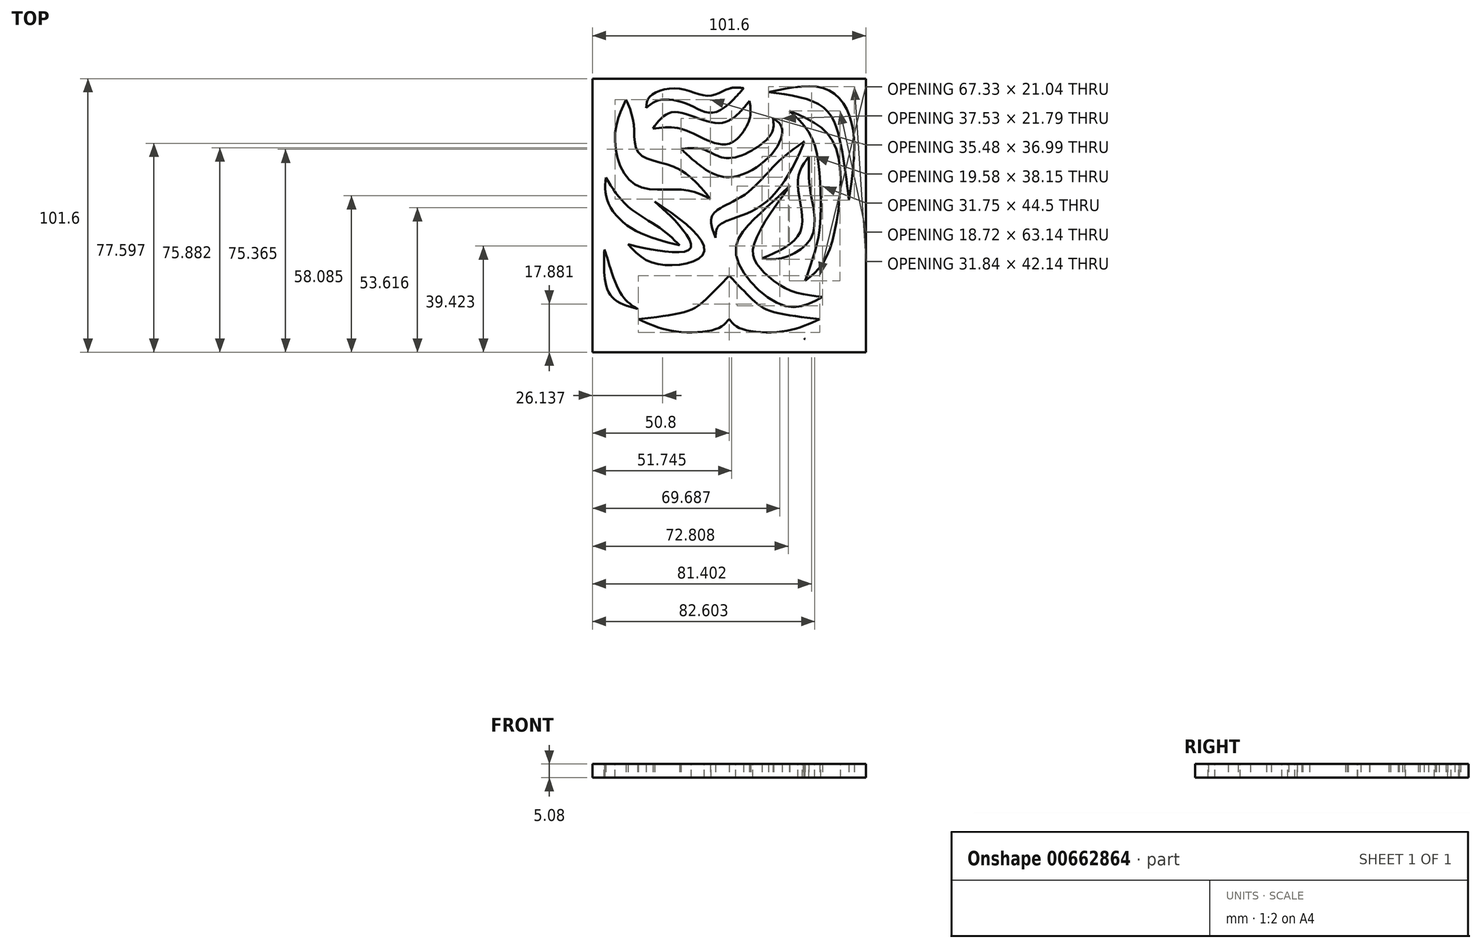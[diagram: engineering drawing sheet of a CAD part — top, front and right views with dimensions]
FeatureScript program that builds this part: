
annotation { "Feature Type Name" : "Feature", "Feature Type Description" : "" }
export const myFeature = defineFeature(function(context is Context, id is Id, definition is map)
    precondition{}
    {
        {
            var Q0;
            Q0=qCreatedBy(makeId("Top.planeOp"),FACE);
            var sketch = newSketch(context, id + "F0", { "sketchPlane" : qUnion([Q0])});
            skLineSegment(sketch, "E0.bottom", {"start": v(50.8, 50.8) * mm, "end": v(-50.8, 50.8) * mm});
            skLineSegment(sketch, "E0.top", {"start": v(50.8, -50.8) * mm, "end": v(-50.8, -50.8) * mm});
            skLineSegment(sketch, "E0.left", {"start": v(50.8, 50.8) * mm, "end": v(50.8, -50.8) * mm});
            skLineSegment(sketch, "E0.right", {"start": v(-50.8, 50.8) * mm, "end": v(-50.8, -50.8) * mm});
            skPoint(sketch, "E0.middle", {"position": v(0, 0) * mm});
            skFitSpline(sketch, "E1", {"points": [v(-38.26, 43.06) * mm, v(-42.4, 28.82) * mm, v(-35, 11.48) * mm, v(-17.34, 9.57) * mm, v(-6.92, 6.07) * mm], "startDerivative": vector(-24.94, -52.93) * mm, "endDerivative": vector(43.77, -22.42) * mm});
            skFitSpline(sketch, "E2", {"points": [v(-38.26, 43.06) * mm, v(-35.4, 33.75) * mm, v(-33.5, 23.1) * mm, v(-19.81, 17.76) * mm, v(-6.92, 6.07) * mm], "startDerivative": vector(17.36, -40) * mm, "endDerivative": vector(39.04, -48.3) * mm});
            skFitSpline(sketch, "E3", {"points": [v(-28.32, 32.16) * mm, v(-20.6, 38.37) * mm, v(-3.58, 34.3) * mm, v(7.55, 42.5) * mm], "startDerivative": vector(22.21, 31.48) * mm, "endDerivative": vector(28.77, 35.63) * mm});
            skFitSpline(sketch, "E4", {"points": [v(7.55, 42.5) * mm, v(7.55, 35.66) * mm, v(0, 26.67) * mm, v(-11.3, 29.46) * mm, v(-20.37, 32.64) * mm, v(-28.32, 32.16) * mm], "startDerivative": vector(6.77, -37) * mm, "endDerivative": vector(-43.42, -6.58) * mm});
            skFitSpline(sketch, "E5", {"points": [v(-17.82, 24.68) * mm, v(-9.31, 24.45) * mm, v(0, 21.26) * mm, v(15.43, 29.93) * mm, v(16.3, 35.98) * mm], "startDerivative": vector(38.3, 4.27) * mm, "endDerivative": vector(-4.66, 29.53) * mm});
            skFitSpline(sketch, "E6", {"points": [v(16.3, 35.98) * mm, v(19.56, 32.8) * mm, v(16.3, 23.33) * mm, v(0, 14.19) * mm, v(-11.46, 19.04) * mm, v(-17.82, 24.68) * mm], "startDerivative": vector(31.19, -18.81) * mm, "endDerivative": vector(-31.98, 30.34) * mm});
            skFitSpline(sketch, "E7", {"points": [v(-45.82, 14.03) * mm, v(-45.26, 5.67) * mm, v(-36.75, -4.5) * mm, v(-18.38, -11.1) * mm], "startDerivative": vector(-2.37, -31.1) * mm, "endDerivative": vector(49.48, -12.28) * mm});
            skFitSpline(sketch, "E8", {"points": [v(-18.38, -11.1) * mm, v(-25.14, -5.06) * mm, v(-37.39, 3.2) * mm, v(-45.82, 14.03) * mm], "startDerivative": vector(-20.78, 21.33) * mm, "endDerivative": vector(-20.77, 32.88) * mm});
            skFitSpline(sketch, "E9", {"points": [v(-27.6, 5.12) * mm, v(-18.54, -3.71) * mm, v(-14.4, -12.38) * mm, v(-28.64, -12.7) * mm, v(-37.47, -10.71) * mm], "startDerivative": vector(33.91, -29.82) * mm, "endDerivative": vector(-32.2, 8.68) * mm});
            skFitSpline(sketch, "E10", {"points": [v(-37.47, -10.71) * mm, v(-30.63, -16.68) * mm, v(-18.78, -18.35) * mm, v(-9.63, -14.53) * mm, v(-11.3, -7.93) * mm, v(-27.6, 5.12) * mm], "startDerivative": vector(33.66, -38) * mm, "endDerivative": vector(-71.79, 48.43) * mm});
            skFitSpline(sketch, "E11", {"points": [v(-43.45, -12.76) * mm, v(-35.26, -21.02) * mm, v(-18.3, -24.64) * mm, v(0, -8.26) * mm], "startDerivative": vector(24.8, -32.16) * mm, "endDerivative": vector(43.21, 55.04) * mm});
            skFitSpline(sketch, "E12", {"points": [v(0, -8.26) * mm, v(-3.36, -19.35) * mm, v(-14.74, -32.4) * mm, v(-26.27, -34.07) * mm, v(-37.14, -27.69) * mm, v(-43.45, -12.76) * mm], "startDerivative": vector(-11.25, -58.13) * mm, "endDerivative": vector(-21.7, 76.53) * mm});
            skFitSpline(sketch, "E13", {"points": [v(-5.03, -8.26) * mm, v(-3.5, -3.55) * mm, v(14.83, 5.94) * mm, v(27.8, 27.47) * mm, v(27.44, 27.11) * mm], "startDerivative": vector(0.93, 29.14) * mm, "endDerivative": vector(-8.43, -11.17) * mm});
            skFitSpline(sketch, "E14", {"points": [v(27.44, 27.11) * mm, v(17.37, 19.06) * mm, v(5.19, 7.32) * mm, v(-6.2, 0) * mm, v(-5.03, -8.26) * mm], "startDerivative": vector(-40.62, -28.64) * mm, "endDerivative": vector(17.62, -44.65) * mm});
            skFitSpline(sketch, "E15", {"points": [v(29.69, 21.9) * mm, v(25.56, 12.69) * mm, v(26.65, -5.5) * mm, v(12.22, -15.95) * mm], "startDerivative": vector(-21.82, -28.94) * mm, "endDerivative": vector(-52.75, -22.05) * mm});
            skFitSpline(sketch, "E16", {"points": [v(12.22, -15.95) * mm, v(19.18, -15.95) * mm, v(30.56, -8.2) * mm, v(30.85, 5.44) * mm, v(29.69, 14) * mm, v(29.69, 21.9) * mm], "startDerivative": vector(37.4, -5.69) * mm, "endDerivative": vector(1.26, 45) * mm});
            skFitSpline(sketch, "E17", {"points": [v(22.51, 10.87) * mm, v(10.77, 0) * mm, v(2.58, -14.28) * mm, v(20.34, -33.49) * mm, v(34.76, -30.23) * mm], "startDerivative": vector(-48.23, -44.33) * mm, "endDerivative": vector(58.75, 32.84) * mm});
            skFitSpline(sketch, "E18", {"points": [v(34.76, -30.23) * mm, v(21.79, -27.47) * mm, v(11.71, -19.79) * mm, v(8.89, -12.54) * mm, v(22.51, 10.87) * mm], "startDerivative": vector(-55.74, 5.82) * mm, "endDerivative": vector(56.53, 78.04) * mm});
            skFitSpline(sketch, "E19", {"points": [v(14.68, 45.81) * mm, v(36.5, 46.75) * mm, v(45.78, 33.34) * mm, v(44.55, 5.73) * mm], "startDerivative": vector(72.4, 15.06) * mm, "endDerivative": vector(-11.52, -78.01) * mm});
            skFitSpline(sketch, "E20", {"points": [v(44.55, 5.73) * mm, v(41.65, 25.66) * mm, v(35.42, 39.8) * mm, v(14.68, 45.81) * mm], "startDerivative": vector(-7.4, 59.2) * mm, "endDerivative": vector(-68.23, 9.05) * mm});
            skFitSpline(sketch, "E21", {"points": [v(22.44, 38.85) * mm, v(31.14, 27.9) * mm, v(34.04, 5.87) * mm, v(32.95, -9.13) * mm, v(28.24, -24.28) * mm], "startDerivative": vector(43.9, -40) * mm, "endDerivative": vector(-22.82, -63.16) * mm});
            skFitSpline(sketch, "E22", {"points": [v(28.24, -24.28) * mm, v(35.13, -17.32) * mm, v(40.7, 2.97) * mm, v(38.24, 28.13) * mm, v(22.44, 38.85) * mm], "startDerivative": vector(40.52, 31.02) * mm, "endDerivative": vector(-73.62, 31.13) * mm});
            skFitSpline(sketch, "E23", {"points": [v(-30.84, 39.94) * mm, v(-25.69, 42.84) * mm, v(-14.82, 41.1) * mm, v(-4.45, 38.56) * mm, v(5.26, 47.12) * mm, v(5.4, 47.26) * mm], "startDerivative": vector(23.98, 19.64) * mm, "endDerivative": vector(2.28, 1.74) * mm});
            skFitSpline(sketch, "E24", {"points": [v(5.4, 47.26) * mm, v(0, 47.12) * mm, v(-7.2, 44.43) * mm, v(-18.95, 47.12) * mm, v(-29.35, 44.29) * mm, v(-30.84, 39.94) * mm], "startDerivative": vector(-32.13, 3.94) * mm, "endDerivative": vector(-2.61, -30.14) * mm});
            skFitSpline(sketch, "E25", {"points": [v(0, -22.4) * mm, v(-7.93, -30.52) * mm, v(-14.45, -35.16) * mm, v(-33.66, -38.49) * mm], "startDerivative": vector(-26.34, -27.38) * mm, "endDerivative": vector(-53.13, -5.62) * mm});
            skFitSpline(sketch, "E26", {"points": [v(-33.66, -38.49) * mm, v(-20.62, -42.98) * mm, v(-4.02, -41.9) * mm, v(0, -38.49) * mm], "startDerivative": vector(32.02, -15.06) * mm, "endDerivative": vector(12.77, 16.62) * mm});
            skLineSegment(sketch, "E27", {"start": v(0, 0) * mm, "end": v(0, -50.8) * mm});
            skFitSpline(sketch, "E28.MirrorCS", {"points": [v(33.66, -38.49) * mm, v(20.62, -42.98) * mm, v(4.02, -41.9) * mm, v(0, -38.49) * mm], "startDerivative": vector(-32.02, -15.06) * mm, "endDerivative": vector(-12.77, 16.62) * mm});
            skFitSpline(sketch, "E29.MirrorCS", {"points": [v(0, -22.4) * mm, v(7.93, -30.52) * mm, v(14.45, -35.16) * mm, v(33.66, -38.49) * mm], "startDerivative": vector(26.34, -27.38) * mm, "endDerivative": vector(53.13, -5.62) * mm});
            skFitSpline(sketch, "E30", {"points": [v(44.48, -19.79) * mm, v(41.65, -31.9) * mm, v(33.31, -43.56) * mm, v(27.95, -45.81) * mm, v(28.02, -45.3) * mm], "startDerivative": vector(-5.36, -35.43) * mm, "endDerivative": vector(3.99, 8.97) * mm});
            skFitSpline(sketch, "E31", {"points": [v(27.95, -45.81) * mm, v(38.53, -45.81) * mm, v(46.94, -32.11) * mm, v(44.48, -19.79) * mm], "startDerivative": vector(36.24, -8.88) * mm, "endDerivative": vector(-14.28, 35.15) * mm});
            skFitSpline(sketch, "E32", {"points": [v(-33.95, -34.72) * mm, v(-40.98, -27.69) * mm, v(-46.28, -12.76) * mm, v(-46.35, -12.76) * mm], "startDerivative": vector(-17.27, 10.34) * mm, "endDerivative": vector(-1.77, -1.13) * mm});
            skFitSpline(sketch, "E33", {"points": [v(-46.35, -12.76) * mm, v(-46.35, -21.53) * mm, v(-43.45, -30.37) * mm, v(-33.95, -34.72) * mm], "startDerivative": vector(-1.13, -26.61) * mm, "endDerivative": vector(31.59, -8.55) * mm});
            skFitSpline(sketch, "E34", {"points": [v(0, 0) * mm, v(0, 50.8) * mm], "startDerivative": vector(0, 50.8) * mm, "endDerivative": vector(0, 50.8) * mm});
            skSolve(sketch);
        }
        {
            var Q0;
            {var subQ14=sQuery(id+"F0.wireOp",EDGE,"E0.right");Q0=makeQuery(id+"F0.imprint","IMPRINT",FACE,{"disambiguationData":[TD([[makeQuery(id+"F0.imprint","IMPRINT",EDGE,{"derivedFrom":subQ14}),1.0]])]});}
            var Q1;
            Q1=makeQuery(id+"F0.imprint","IMPRINT",FACE,{"disambiguationData":[TD([[makeQuery(id+"F0.imprint","IMPRINT",EDGE,{"derivedFrom":sQuery(id+"F0.wireOp",EDGE,"E11")}),-1.0]])]});
            extrude(context, id + "F1", {"entities" : qUnion([Q0, Q1]), "depth" : 5.08 * mm, "offsetDistance" : 25.4 * mm});
        }
        {
            var Q0;
            {var subQ20=sQuery(id+"F0.wireOp",EDGE,"E0.left");Q0=makeQuery(id+"F0.imprint","IMPRINT",FACE,{"disambiguationData":[TD([[makeQuery(id+"F0.imprint","IMPRINT",EDGE,{"derivedFrom":subQ20}),-1.0]])]});}
            var Q1;
            {var subQ0=sQuery(id+"F0.wireOp",EDGE,"E31");var subQ1=sQuery(id+"F0.wireOp",EDGE,"E30");var subQ2=makeQuery(id+"F0.imprint","INTERSECT",VERTEX,{"disambiguationData":[OD(0.0)],"derivedFrom":[subQ1,subQ0]});Q1=makeQuery(id+"F0.imprint","IMPRINT",FACE,{"disambiguationData":[TD([[makeQuery(id+"F0.imprint","IMPRINT",EDGE,{"disambiguationData":[TD([[subQ2,-1.0]])],"derivedFrom":subQ1}),1.0]])]});}
            extrude(context, id + "F2", {"entities" : qUnion([Q0, Q1]), "operationType" : NewBodyOperationType.ADD, "depth" : 5.08 * mm, "offsetDistance" : 25.4 * mm});
        }
    });
